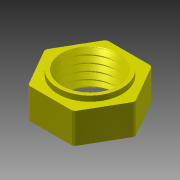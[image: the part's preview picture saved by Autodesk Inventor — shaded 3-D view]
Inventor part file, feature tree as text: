
AUTODESK INVENTOR PART (.ipt)
format: ipt  version: 2013 (Build 170138000, 138)  size: 230,400 bytes
history: native  units: mm
features: sketch x7, extrude x6, helix x1, projected_geometry x1
ambient origin geometry x8: Origin, YZ Plane, XZ Plane, XY Plane, X Axis, Y Axis, Z Axis, Center Point
bodies: Solid1 (feature_tree)
feature tree (15):
  extrude  "Extrusion1"  Depth=10.0mm TaperAngle=0.0deg
  extrude  "Extrusion2"  Depth=15.0mm TaperAngle=0.0deg
  helix  "Coil1"  [1 undecoded]
  extrude  "Extrusion8"  Depth=18.0mm
  extrude  "Extrusion9"  Depth=5.0mm
  extrude  "Extrusion10"  Depth=22.0mm
  extrude  "Extrusion11"  [1 undecoded]
  sketch  "Sketch1"  dims[d0=25.0mm d2=10.0mm d3=0.0mm]
  sketch  "Sketch2"  dims[d4=13.9mm d9=15.0mm d10=0.0mm d11=2.0mm]
  sketch  "Sketch3"  dims[d12=2.0001mm d13=10.0mm d14=100.0mm d15=0.0mm d16=90.0deg d17=90.0deg d18=0.0mm d19=0.0mm d47=18.0mm]
  sketch  "Sketch9"  dims[d49=1.5mm d50=0.0mm d51=5.0mm d52=-7.853982mm]
  sketch  "Sketch10"  dims[d53=5.0mm d54=-7.853982mm d55=22.0mm]
  sketch  "Sketch11"  dims[d56=0.0mm d57=0.0mm]
  sketch  "Sketch12"
  projected_geometry  "Project Cut Edges1"
note: 2 required parameter values undecoded (feature->parameter linkage not recoverable at this tier; creation-order binding heuristic only, values carry confidence <= 0.55)
